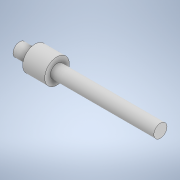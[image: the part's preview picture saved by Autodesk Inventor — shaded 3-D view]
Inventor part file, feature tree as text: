
AUTODESK INVENTOR PART (.ipt)
format: ipt  version: 2021 (Build 250183000, 183)  size: 108,544 bytes
history: native  units: in
note: dims shown in document units (in); Inventor stores cm internally (conversion verified against a paired STEP export)
features: extrude x3, sketch x3
ambient origin geometry x8: Origin, YZ Plane, XZ Plane, XY Plane, X Axis, Y Axis, Z Axis, Center Point
bodies: Solid1 (feature_tree)
feature tree (6):
  extrude  "Extrusion1"  Depth=0.1969in TaperAngle=0.0deg
  extrude  "Extrusion2"  Depth=0.9252in TaperAngle=0.0deg
  extrude  "Extrusion3"  Depth=0.1378in TaperAngle=0.0deg
  sketch  "Sketch1"  dims[d0=0.2205in d1=0.1969in d2=0.0in]
  sketch  "Sketch2"  dims[d3=0.1181in d4=0.9252in d5=0.0in]
  sketch  "Sketch3"  dims[d6=0.1181in d7=0.1378in d8=0.0in]
